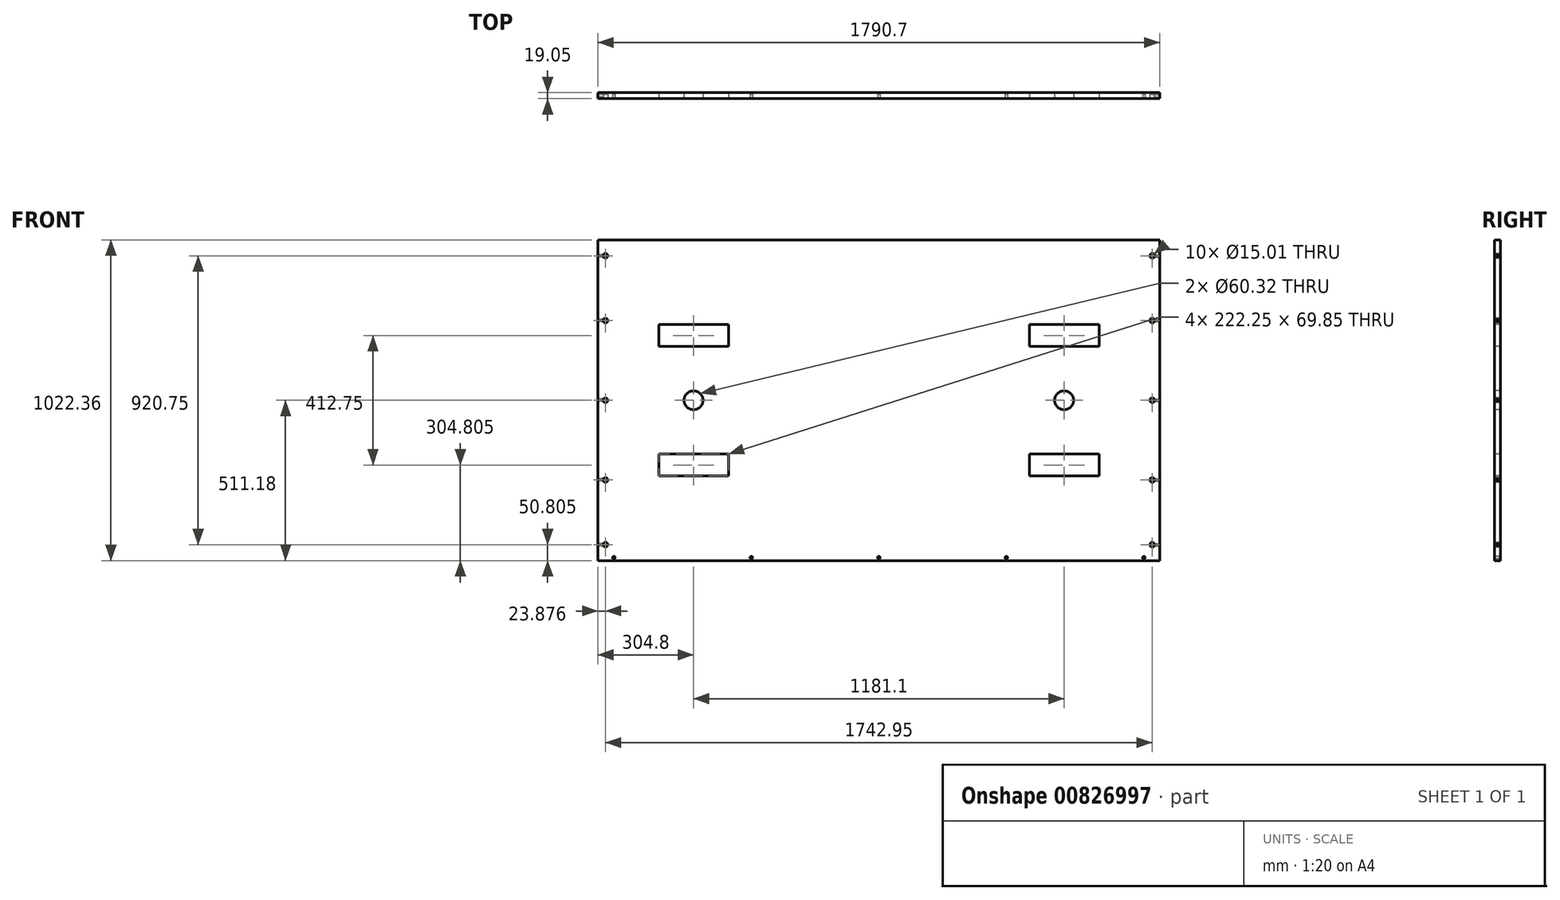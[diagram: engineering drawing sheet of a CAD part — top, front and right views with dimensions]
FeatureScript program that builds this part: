
annotation { "Feature Type Name" : "Feature", "Feature Type Description" : "" }
export const myFeature = defineFeature(function(context is Context, id is Id, definition is map)
    precondition{}
    {
        {
            var Q0;
            Q0=qCreatedBy(makeId("Front.planeOp"),FACE);
            var sketch = newSketch(context, id + "F0", { "sketchPlane" : qUnion([Q0])});
            skLineSegment(sketch, "E0.bottom", {"start": v(-895.35, 511.18) * mm, "end": v(895.35, 511.18) * mm});
            skLineSegment(sketch, "E0.top", {"start": v(-895.35, -511.18) * mm, "end": v(895.35, -511.18) * mm});
            skLineSegment(sketch, "E0.left", {"start": v(-895.35, 511.18) * mm, "end": v(-895.35, -511.18) * mm});
            skLineSegment(sketch, "E0.right", {"start": v(895.35, 511.18) * mm, "end": v(895.35, -511.18) * mm});
            skPoint(sketch, "E0.middle", {"position": v(0, 0) * mm});
            skSolve(sketch);
        }
        {
            var Q0;
            Q0=makeQuery(id+"F0.imprint","IMPRINT",FACE,{"disambiguationData":[TD([[makeQuery(id+"F0.imprint","IMPRINT",EDGE,{"derivedFrom":sQuery(id+"F0.wireOp",EDGE,"E0.bottom")}),-1.0]])]});
            extrude(context, id + "F1", {"entities" : qUnion([Q0]), "depth" : 19.05 * mm, "offsetDistance" : 25.4 * mm});
        }
        {
            var Q0;
            Q0=makeQuery(id+"F1.opExtrude","CAP_FACE",FACE,{"disambiguationData":[OSD([sQuery(id+"F0.wireOp",EDGE,"E0.bottom"),sQuery(id+"F0.wireOp",EDGE,"E0.top"),sQuery(id+"F0.wireOp",EDGE,"E0.left"),sQuery(id+"F0.wireOp",EDGE,"E0.right")])],"isStart":false});
            var sketch = newSketch(context, id + "F2", { "sketchPlane" : qUnion([Q0])});
            skLineSegment(sketch, "E1.bottom", {"start": v(-895.35, 511.18) * mm, "end": v(-590.55, 511.18) * mm});
            skLineSegment(sketch, "E1.top", {"start": v(-895.35, 206.38) * mm, "end": v(-590.55, 206.38) * mm});
            skLineSegment(sketch, "E1.left", {"start": v(-895.35, 511.18) * mm, "end": v(-895.35, 206.38) * mm});
            skLineSegment(sketch, "E1.right", {"start": v(-590.55, 511.18) * mm, "end": v(-590.55, 206.38) * mm});
            skLineSegment(sketch, "E2.bottom", {"start": v(895.35, 511.18) * mm, "end": v(590.55, 511.18) * mm});
            skLineSegment(sketch, "E2.top", {"start": v(895.35, 206.38) * mm, "end": v(590.55, 206.38) * mm});
            skLineSegment(sketch, "E2.left", {"start": v(895.35, 511.18) * mm, "end": v(895.35, 206.38) * mm});
            skLineSegment(sketch, "E2.right", {"start": v(590.55, 511.18) * mm, "end": v(590.55, 206.38) * mm});
            skLineSegment(sketch, "E3.bottom", {"start": v(-895.35, -511.18) * mm, "end": v(-590.55, -511.18) * mm});
            skLineSegment(sketch, "E3.top", {"start": v(-895.35, -206.38) * mm, "end": v(-590.55, -206.38) * mm});
            skLineSegment(sketch, "E3.left", {"start": v(-895.35, -511.18) * mm, "end": v(-895.35, -206.38) * mm});
            skLineSegment(sketch, "E3.right", {"start": v(-590.55, -511.18) * mm, "end": v(-590.55, -206.38) * mm});
            skLineSegment(sketch, "E4.bottom", {"start": v(895.35, -511.18) * mm, "end": v(590.55, -511.18) * mm});
            skLineSegment(sketch, "E4.top", {"start": v(895.35, -206.38) * mm, "end": v(590.55, -206.38) * mm});
            skLineSegment(sketch, "E4.left", {"start": v(895.35, -511.18) * mm, "end": v(895.35, -206.38) * mm});
            skLineSegment(sketch, "E4.right", {"start": v(590.55, -511.18) * mm, "end": v(590.55, -206.38) * mm});
            skLineSegment(sketch, "E5.bottom", {"start": v(-479.43, 241.3) * mm, "end": v(-701.68, 241.3) * mm});
            skLineSegment(sketch, "E5.top", {"start": v(-479.43, 171.45) * mm, "end": v(-701.68, 171.45) * mm});
            skLineSegment(sketch, "E5.left", {"start": v(-479.43, 241.3) * mm, "end": v(-479.43, 171.45) * mm});
            skLineSegment(sketch, "E5.right", {"start": v(-701.68, 241.3) * mm, "end": v(-701.68, 171.45) * mm});
            skPoint(sketch, "E5.middle", {"position": v(-590.55, 206.38) * mm});
            skLineSegment(sketch, "E6.bottom", {"start": v(-701.68, -171.45) * mm, "end": v(-479.43, -171.45) * mm});
            skLineSegment(sketch, "E6.top", {"start": v(-701.68, -241.3) * mm, "end": v(-479.43, -241.3) * mm});
            skLineSegment(sketch, "E6.left", {"start": v(-701.68, -171.45) * mm, "end": v(-701.68, -241.3) * mm});
            skLineSegment(sketch, "E6.right", {"start": v(-479.43, -171.45) * mm, "end": v(-479.43, -241.3) * mm});
            skPoint(sketch, "E6.middle", {"position": v(-590.55, -206.38) * mm});
            skLineSegment(sketch, "E7.bottom", {"start": v(701.68, 241.3) * mm, "end": v(479.43, 241.3) * mm});
            skLineSegment(sketch, "E7.top", {"start": v(701.68, 171.45) * mm, "end": v(479.43, 171.45) * mm});
            skLineSegment(sketch, "E7.left", {"start": v(701.68, 241.3) * mm, "end": v(701.68, 171.45) * mm});
            skLineSegment(sketch, "E7.right", {"start": v(479.43, 241.3) * mm, "end": v(479.43, 171.45) * mm});
            skPoint(sketch, "E7.middle", {"position": v(590.55, 206.38) * mm});
            skLineSegment(sketch, "E8.bottom", {"start": v(479.42, -171.45) * mm, "end": v(701.67, -171.45) * mm});
            skLineSegment(sketch, "E8.top", {"start": v(479.42, -241.3) * mm, "end": v(701.67, -241.3) * mm});
            skLineSegment(sketch, "E8.left", {"start": v(479.42, -171.45) * mm, "end": v(479.42, -241.3) * mm});
            skLineSegment(sketch, "E8.right", {"start": v(701.67, -171.45) * mm, "end": v(701.67, -241.3) * mm});
            skPoint(sketch, "E8.middle", {"position": v(590.55, -206.38) * mm});
            skLineSegment(sketch, "E9", {"start": v(-895.35, 0) * mm, "end": v(-590.55, 0) * mm});
            skLineSegment(sketch, "E10", {"start": v(895.35, 0) * mm, "end": v(590.55, 0) * mm});
            skCircle(sketch, "E11", {"center": v(-590.55, 0) * mm, "radius": 30.16 * mm});
            skCircle(sketch, "E12", {"center": v(590.55, 0) * mm, "radius": 30.16 * mm});
            skSolve(sketch);
        }
        {
            var Q0;
            {var subQ0=sQuery(id+"F2.wireOp",EDGE,"E5.top");Q0=makeQuery(id+"F2.imprint","IMPRINT",FACE,{"disambiguationData":[TD([[makeQuery(id+"F2.imprint","IMPRINT",EDGE,{"derivedFrom":subQ0}),-1.0]])]});}
            var Q1;
            {var subQ0=sQuery(id+"F2.wireOp",EDGE,"E1.right");var subQ1=sQuery(id+"F2.wireOp",EDGE,"E1.top");var subQ2=makeQuery(id+"F2.imprint","INTERSECT",VERTEX,{"derivedFrom":[subQ1,subQ0]});Q1=makeQuery(id+"F2.imprint","IMPRINT",FACE,{"disambiguationData":[TD([[makeQuery(id+"F2.imprint","IMPRINT",EDGE,{"disambiguationData":[TD([[subQ2,1.0]])],"derivedFrom":subQ1}),1.0]])]});}
            var Q2;
            {var subQ6=sQuery(id+"F2.wireOp",EDGE,"E7.top");Q2=makeQuery(id+"F2.imprint","IMPRINT",FACE,{"disambiguationData":[TD([[makeQuery(id+"F2.imprint","IMPRINT",EDGE,{"derivedFrom":subQ6}),-1.0]])]});}
            var Q3;
            {var subQ0=sQuery(id+"F2.wireOp",EDGE,"E2.right");var subQ1=sQuery(id+"F2.wireOp",EDGE,"E2.top");var subQ2=makeQuery(id+"F2.imprint","INTERSECT",VERTEX,{"derivedFrom":[subQ1,subQ0]});Q3=makeQuery(id+"F2.imprint","IMPRINT",FACE,{"disambiguationData":[TD([[makeQuery(id+"F2.imprint","IMPRINT",EDGE,{"disambiguationData":[TD([[subQ2,1.0]])],"derivedFrom":subQ1}),-1.0]])]});}
            var Q4;
            Q4=makeQuery(id+"F2.imprint","IMPRINT",FACE,{"disambiguationData":[TD([[makeQuery(id+"F2.imprint","IMPRINT",EDGE,{"derivedFrom":sQuery(id+"F2.wireOp",EDGE,"E12")}),1.0]])]});
            var Q5;
            Q5=makeQuery(id+"F2.imprint","IMPRINT",FACE,{"disambiguationData":[TD([[makeQuery(id+"F2.imprint","IMPRINT",EDGE,{"derivedFrom":sQuery(id+"F2.wireOp",EDGE,"E11")}),1.0]])]});
            var Q6;
            {var subQ0=sQuery(id+"F2.wireOp",EDGE,"E6.bottom");Q6=makeQuery(id+"F2.imprint","IMPRINT",FACE,{"disambiguationData":[TD([[makeQuery(id+"F2.imprint","IMPRINT",EDGE,{"derivedFrom":subQ0}),-1.0]])]});}
            var Q7;
            {var subQ0=sQuery(id+"F2.wireOp",EDGE,"E3.right");var subQ1=sQuery(id+"F2.wireOp",EDGE,"E3.top");var subQ2=makeQuery(id+"F2.imprint","INTERSECT",VERTEX,{"derivedFrom":[subQ1,subQ0]});Q7=makeQuery(id+"F2.imprint","IMPRINT",FACE,{"disambiguationData":[TD([[makeQuery(id+"F2.imprint","IMPRINT",EDGE,{"disambiguationData":[TD([[subQ2,1.0]])],"derivedFrom":subQ1}),-1.0]])]});}
            var Q8;
            {var subQ0=sQuery(id+"F2.wireOp",EDGE,"E8.bottom");Q8=makeQuery(id+"F2.imprint","IMPRINT",FACE,{"disambiguationData":[TD([[makeQuery(id+"F2.imprint","IMPRINT",EDGE,{"derivedFrom":subQ0}),-1.0]])]});}
            var Q9;
            {var subQ0=sQuery(id+"F2.wireOp",EDGE,"E4.right");var subQ1=sQuery(id+"F2.wireOp",EDGE,"E4.top");var subQ2=makeQuery(id+"F2.imprint","INTERSECT",VERTEX,{"derivedFrom":[subQ1,subQ0]});Q9=makeQuery(id+"F2.imprint","IMPRINT",FACE,{"disambiguationData":[TD([[makeQuery(id+"F2.imprint","IMPRINT",EDGE,{"disambiguationData":[TD([[subQ2,1.0]])],"derivedFrom":subQ1}),1.0]])]});}
            extrude(context, id + "F3", {"entities" : qUnion([Q0, Q1, Q2, Q3, Q4, Q5, Q6, Q7, Q8, Q9]), "operationType" : NewBodyOperationType.REMOVE, "oppositeDirection" : true, "depth" : 25.4 * mm, "offsetDistance" : 25.4 * mm});
        }
        {
            var Q0;
            Q0=makeQuery(id+"F1.opExtrude","CAP_FACE",FACE,{"disambiguationData":[OSD([sQuery(id+"F0.wireOp",EDGE,"E0.bottom"),sQuery(id+"F0.wireOp",EDGE,"E0.top"),sQuery(id+"F0.wireOp",EDGE,"E0.left"),sQuery(id+"F0.wireOp",EDGE,"E0.right")])],"isStart":false});
            var sketch = newSketch(context, id + "F4", { "sketchPlane" : qUnion([Q0])});
            skLineSegment(sketch, "E13", {"start": v(-895.35, 511.18) * mm, "end": v(-895.35, 460.38) * mm});
            skLineSegment(sketch, "E14", {"start": v(-895.35, 460.38) * mm, "end": v(-871.47, 460.38) * mm});
            skLineSegment(sketch, "E15", {"start": v(-895.35, -511.18) * mm, "end": v(-895.35, -460.38) * mm});
            skLineSegment(sketch, "E16", {"start": v(-895.35, -460.38) * mm, "end": v(-871.47, -460.38) * mm});
            skLineSegment(sketch, "E17", {"start": v(-895.35, 0) * mm, "end": v(-871.47, 0) * mm});
            skLineSegment(sketch, "E18", {"start": v(895.35, 511.18) * mm, "end": v(895.35, 460.38) * mm});
            skLineSegment(sketch, "E19", {"start": v(895.35, 460.38) * mm, "end": v(871.47, 460.38) * mm});
            skLineSegment(sketch, "E20", {"start": v(895.35, 0) * mm, "end": v(871.47, 0) * mm});
            skLineSegment(sketch, "E21", {"start": v(895.35, -511.18) * mm, "end": v(895.35, -460.38) * mm});
            skLineSegment(sketch, "E22", {"start": v(895.35, -460.38) * mm, "end": v(871.47, -460.38) * mm});
            skLineSegment(sketch, "E23", {"start": v(871.47, 0) * mm, "end": v(871.47, 254) * mm});
            skLineSegment(sketch, "E24", {"start": v(871.47, 0) * mm, "end": v(871.47, -254) * mm});
            skLineSegment(sketch, "E25", {"start": v(-871.47, 0) * mm, "end": v(-871.47, 254) * mm});
            skLineSegment(sketch, "E26", {"start": v(-871.47, 0) * mm, "end": v(-871.47, -254) * mm});
            skSolve(sketch);
        }
        {
            var Q0;
            Q0=sQuery(id+"F4.wireOp",VERTEX,"E14.end");
            var Q1;
            Q1=sQuery(id+"F4.wireOp",VERTEX,"E17.end");
            var Q2;
            Q2=sQuery(id+"F4.wireOp",VERTEX,"E16.end");
            var Q3;
            Q3=sQuery(id+"F4.wireOp",VERTEX,"E22.end");
            var Q4;
            Q4=sQuery(id+"F4.wireOp",VERTEX,"E20.end");
            var Q5;
            Q5=sQuery(id+"F4.wireOp",VERTEX,"E19.end");
            var Q6;
            Q6=sQuery(id+"F4.wireOp",VERTEX,"E25.end");
            var Q7;
            Q7=sQuery(id+"F4.wireOp",VERTEX,"E26.end");
            var Q8;
            Q8=sQuery(id+"F4.wireOp",VERTEX,"E23.end");
            var Q9;
            Q9=sQuery(id+"F4.wireOp",VERTEX,"E24.end");
            var Q10;
            Q10=makeQuery(id+"F1.opExtrude","SWEPT_BODY",BODY,{"disambiguationData":[OSD([sQuery(id+"F0.wireOp",EDGE,"E0.bottom"),sQuery(id+"F0.wireOp",EDGE,"E0.top"),sQuery(id+"F0.wireOp",EDGE,"E0.left"),sQuery(id+"F0.wireOp",EDGE,"E0.right")])]});
            hole(context, id + "F5", {"style" : HoleStyle.SIMPLE, "endStyle" : HoleEndStyle.BLIND, "holeDiameter" : 15 * mm, "majorDiameter" : 6.35 * mm, "holeDepth" : 14.22 * mm, "isTappedThrough" : true, "tappedDepth" : 12.7 * mm, "tapClearance" : 3, "startFromSketch" : true, "locations" : qUnion([Q0, Q1, Q2, Q3, Q4, Q5, Q6, Q7, Q8, Q9]), "scope" : qUnion([Q10])});
        }
        {
            var Q0;
            Q0=makeQuery(id+"F1.opExtrude","CAP_FACE",FACE,{"disambiguationData":[OSD([sQuery(id+"F0.wireOp",EDGE,"E0.bottom"),sQuery(id+"F0.wireOp",EDGE,"E0.top"),sQuery(id+"F0.wireOp",EDGE,"E0.left"),sQuery(id+"F0.wireOp",EDGE,"E0.right")])],"isStart":false});
            var sketch = newSketch(context, id + "F6", { "sketchPlane" : qUnion([Q0])});
            skLineSegment(sketch, "E27", {"start": v(-895.35, -511.18) * mm, "end": v(-844.55, -511.18) * mm});
            skLineSegment(sketch, "E28", {"start": v(-844.55, -511.18) * mm, "end": v(-844.55, -501.65) * mm});
            skLineSegment(sketch, "E29", {"start": v(895.35, -511.18) * mm, "end": v(844.55, -511.18) * mm});
            skLineSegment(sketch, "E30", {"start": v(844.55, -511.18) * mm, "end": v(844.55, -501.65) * mm});
            skLineSegment(sketch, "E31", {"start": v(0, -511.18) * mm, "end": v(406.4, -511.18) * mm});
            skLineSegment(sketch, "E32", {"start": v(0, -511.18) * mm, "end": v(-406.4, -511.18) * mm});
            skLineSegment(sketch, "E33", {"start": v(-406.4, -511.18) * mm, "end": v(-406.4, -501.65) * mm});
            skLineSegment(sketch, "E34", {"start": v(406.4, -511.18) * mm, "end": v(406.4, -501.65) * mm});
            skLineSegment(sketch, "E35", {"start": v(0, -511.18) * mm, "end": v(0, -501.65) * mm});
            skPoint(sketch, "E36", {"position": v(-844.55, -501.65) * mm});
            skPoint(sketch, "E37", {"position": v(-406.4, -501.65) * mm});
            skPoint(sketch, "E38", {"position": v(0, -501.65) * mm});
            skPoint(sketch, "E39", {"position": v(406.4, -501.65) * mm});
            skPoint(sketch, "E40", {"position": v(844.55, -501.65) * mm});
            skSolve(sketch);
        }
        {
            var Q0;
            Q0=sQuery(id+"F6.wireOp",VERTEX,"E36");
            var Q1;
            Q1=sQuery(id+"F6.wireOp",VERTEX,"E37");
            var Q2;
            Q2=sQuery(id+"F6.wireOp",VERTEX,"E38");
            var Q3;
            Q3=sQuery(id+"F6.wireOp",VERTEX,"E39");
            var Q4;
            Q4=sQuery(id+"F6.wireOp",VERTEX,"E40");
            var Q5;
            Q5=makeQuery(id+"F1.opExtrude","SWEPT_BODY",BODY,{"disambiguationData":[OSD([sQuery(id+"F0.wireOp",EDGE,"E0.bottom"),sQuery(id+"F0.wireOp",EDGE,"E0.top"),sQuery(id+"F0.wireOp",EDGE,"E0.left"),sQuery(id+"F0.wireOp",EDGE,"E0.right")])]});
            hole(context, id + "F7", {"style" : HoleStyle.SIMPLE, "endStyle" : HoleEndStyle.BLIND, "holeDiameter" : 8 * mm, "majorDiameter" : 6.35 * mm, "holeDepth" : 14.22 * mm, "isTappedThrough" : true, "tappedDepth" : 12.7 * mm, "tapClearance" : 3, "startFromSketch" : true, "locations" : qUnion([Q0, Q1, Q2, Q3, Q4]), "scope" : qUnion([Q5])});
        }
        {
            var Q0;
            Q0=makeQuery(id+"F1.opExtrude","SWEPT_FACE",FACE,{"disambiguationData":[OSD([sQuery(id+"F0.wireOp",EDGE,"E0.right")])]});
            var sketch = newSketch(context, id + "F8", { "sketchPlane" : qUnion([Q0])});
            skLineSegment(sketch, "E41", {"start": v(-9.53, 511.18) * mm, "end": v(-9.53, 460.38) * mm});
            skLineSegment(sketch, "E42", {"start": v(-9.53, -511.17) * mm, "end": v(-9.53, -460.37) * mm});
            skLineSegment(sketch, "E43", {"start": v(-19.05, 0) * mm, "end": v(0, 0) * mm});
            skPoint(sketch, "E44", {"position": v(-9.53, 0) * mm});
            skLineSegment(sketch, "E45", {"start": v(-9.53, 0) * mm, "end": v(-9.53, 254) * mm});
            skLineSegment(sketch, "E46", {"start": v(-9.53, 0) * mm, "end": v(-9.53, -254) * mm});
            skPoint(sketch, "E47", {"position": v(-9.53, 254) * mm});
            skPoint(sketch, "E48", {"position": v(-9.53, -254) * mm});
            skSolve(sketch);
        }
        {
            var Q0;
            Q0=sQuery(id+"F8.wireOp",VERTEX,"E41.end");
            var Q1;
            Q1=sQuery(id+"F8.wireOp",VERTEX,"E47");
            var Q2;
            Q2=sQuery(id+"F8.wireOp",VERTEX,"E44");
            var Q3;
            Q3=sQuery(id+"F8.wireOp",VERTEX,"E48");
            var Q4;
            Q4=sQuery(id+"F8.wireOp",VERTEX,"E42.end");
            var Q5;
            Q5=makeQuery(id+"F1.opExtrude","SWEPT_BODY",BODY,{"disambiguationData":[OSD([sQuery(id+"F0.wireOp",EDGE,"E0.bottom"),sQuery(id+"F0.wireOp",EDGE,"E0.top"),sQuery(id+"F0.wireOp",EDGE,"E0.left"),sQuery(id+"F0.wireOp",EDGE,"E0.right")])]});
            hole(context, id + "F9", {"style" : HoleStyle.SIMPLE, "endStyle" : HoleEndStyle.BLIND, "holeDiameter" : 8 * mm, "majorDiameter" : 6.35 * mm, "holeDepth" : 25.4 * mm, "isTappedThrough" : true, "tappedDepth" : 12.7 * mm, "tapClearance" : 3, "startFromSketch" : true, "locations" : qUnion([Q0, Q1, Q2, Q3, Q4]), "scope" : qUnion([Q5])});
        }
        {
            var Q0;
            Q0=makeQuery(id+"F1.opExtrude","SWEPT_FACE",FACE,{"disambiguationData":[OSD([sQuery(id+"F0.wireOp",EDGE,"E0.left")])]});
            var sketch = newSketch(context, id + "F10", { "sketchPlane" : qUnion([Q0])});
            skLineSegment(sketch, "E49", {"start": v(9.53, 511.17) * mm, "end": v(9.53, 460.37) * mm});
            skLineSegment(sketch, "E50", {"start": v(9.53, -511.18) * mm, "end": v(9.53, -460.38) * mm});
            skLineSegment(sketch, "E51", {"start": v(19.05, 0) * mm, "end": v(0, 0) * mm});
            skLineSegment(sketch, "E52", {"start": v(9.53, 0) * mm, "end": v(9.53, -254) * mm});
            skLineSegment(sketch, "E53", {"start": v(9.53, 0) * mm, "end": v(9.53, 254) * mm});
            skSolve(sketch);
        }
        {
            var Q0;
            Q0=sQuery(id+"F10.wireOp",VERTEX,"E49.end");
            var Q1;
            Q1=sQuery(id+"F10.wireOp",VERTEX,"E53.end");
            var Q2;
            Q2=sQuery(id+"F10.wireOp",VERTEX,"E52.start");
            var Q3;
            Q3=sQuery(id+"F10.wireOp",VERTEX,"E52.end");
            var Q4;
            Q4=sQuery(id+"F10.wireOp",VERTEX,"E50.end");
            var Q5;
            Q5=makeQuery(id+"F1.opExtrude","SWEPT_BODY",BODY,{"disambiguationData":[OSD([sQuery(id+"F0.wireOp",EDGE,"E0.bottom"),sQuery(id+"F0.wireOp",EDGE,"E0.top"),sQuery(id+"F0.wireOp",EDGE,"E0.left"),sQuery(id+"F0.wireOp",EDGE,"E0.right")])]});
            hole(context, id + "F11", {"style" : HoleStyle.SIMPLE, "endStyle" : HoleEndStyle.BLIND, "holeDiameter" : 8 * mm, "majorDiameter" : 6.35 * mm, "holeDepth" : 25.4 * mm, "isTappedThrough" : true, "tappedDepth" : 12.7 * mm, "tapClearance" : 3, "startFromSketch" : true, "locations" : qUnion([Q0, Q1, Q2, Q3, Q4]), "scope" : qUnion([Q5])});
        }
    });
